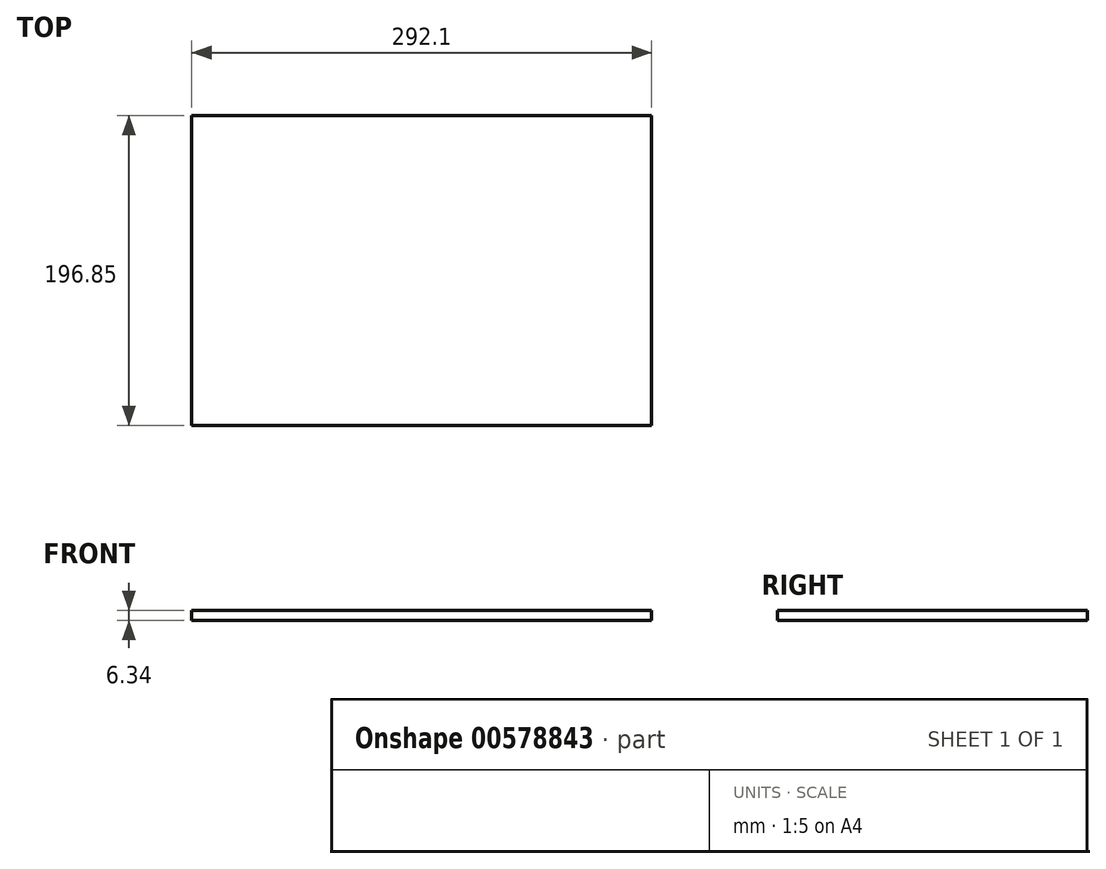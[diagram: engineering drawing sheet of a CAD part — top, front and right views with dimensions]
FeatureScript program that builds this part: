
annotation { "Feature Type Name" : "Feature", "Feature Type Description" : "" }
export const myFeature = defineFeature(function(context is Context, id is Id, definition is map)
    precondition{}
    {
        {
            var Q0;
            Q0=qCreatedBy(makeId("Front.planeOp"),FACE);
            var sketch = newSketch(context, id + "F0", { "sketchPlane" : qUnion([Q0])});
            skLineSegment(sketch, "E0.bottom", {"start": v(146.05, 3.18) * mm, "end": v(-146.05, 3.18) * mm});
            skLineSegment(sketch, "E0.top", {"start": v(146.05, -3.18) * mm, "end": v(-146.05, -3.18) * mm});
            skLineSegment(sketch, "E0.left", {"start": v(146.05, 3.18) * mm, "end": v(146.05, -3.18) * mm});
            skLineSegment(sketch, "E0.right", {"start": v(-146.05, 3.18) * mm, "end": v(-146.05, -3.18) * mm});
            skPoint(sketch, "E0.middle", {"position": v(0, 0) * mm});
            skSolve(sketch);
        }
        {
            var Q0;
            Q0 = qSketchRegion(id + "F0", true);
            extrude(context, id + "F1", {"entities" : qUnion([Q0]), "depth" : 196.85 * mm, "offsetDistance" : 25.4 * mm});
        }
    });
